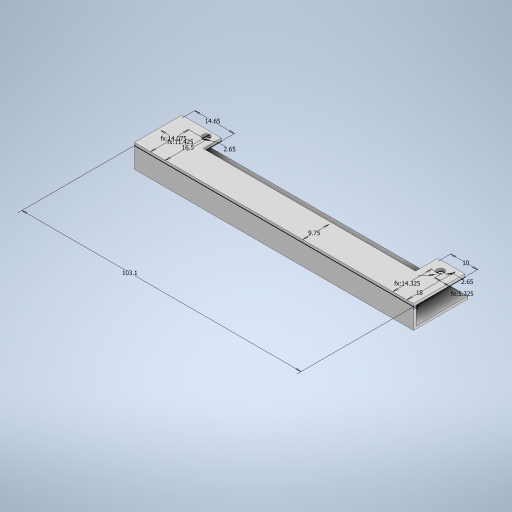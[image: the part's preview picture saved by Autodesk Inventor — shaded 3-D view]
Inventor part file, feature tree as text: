
AUTODESK INVENTOR PART (.ipt)
format: ipt  version: 2023 (Build 270158000, 158)  size: 276,480 bytes
history: native  units: in
note: dims shown in document units (in); Inventor stores cm internally (conversion verified against a paired STEP export)
features: extrude x3, sketch x2
ambient origin geometry x8: Origin, YZ Plane, XZ Plane, XY Plane, X Axis, Y Axis, Z Axis, Center Point
bodies: Solid1 (feature_tree)
feature tree (5):
  sketch  "Sketch1"  dims[d0=0.1043in d1=0.1043in]
  extrude  "Extrusion1"  Depth=0.1043in
  extrude  "Extrusion2"  Depth=0.5768in
  extrude  "Extrusion3"  Depth=0.3937in
  sketch  "Sketch3"  dims[d2=4.0591in d3=0.5768in d4=0.3937in d5=0.7087in d6=0.6496in d7=0.5541in d8=0.4498in d9=0.3839in d10=0.564in d11=0.2096in d12=0.0394in d13=0.0in d14=0.0394in d15=0.2992in d16=0.0in d17=0.0394in d18=0.748in d19=0.0in]
